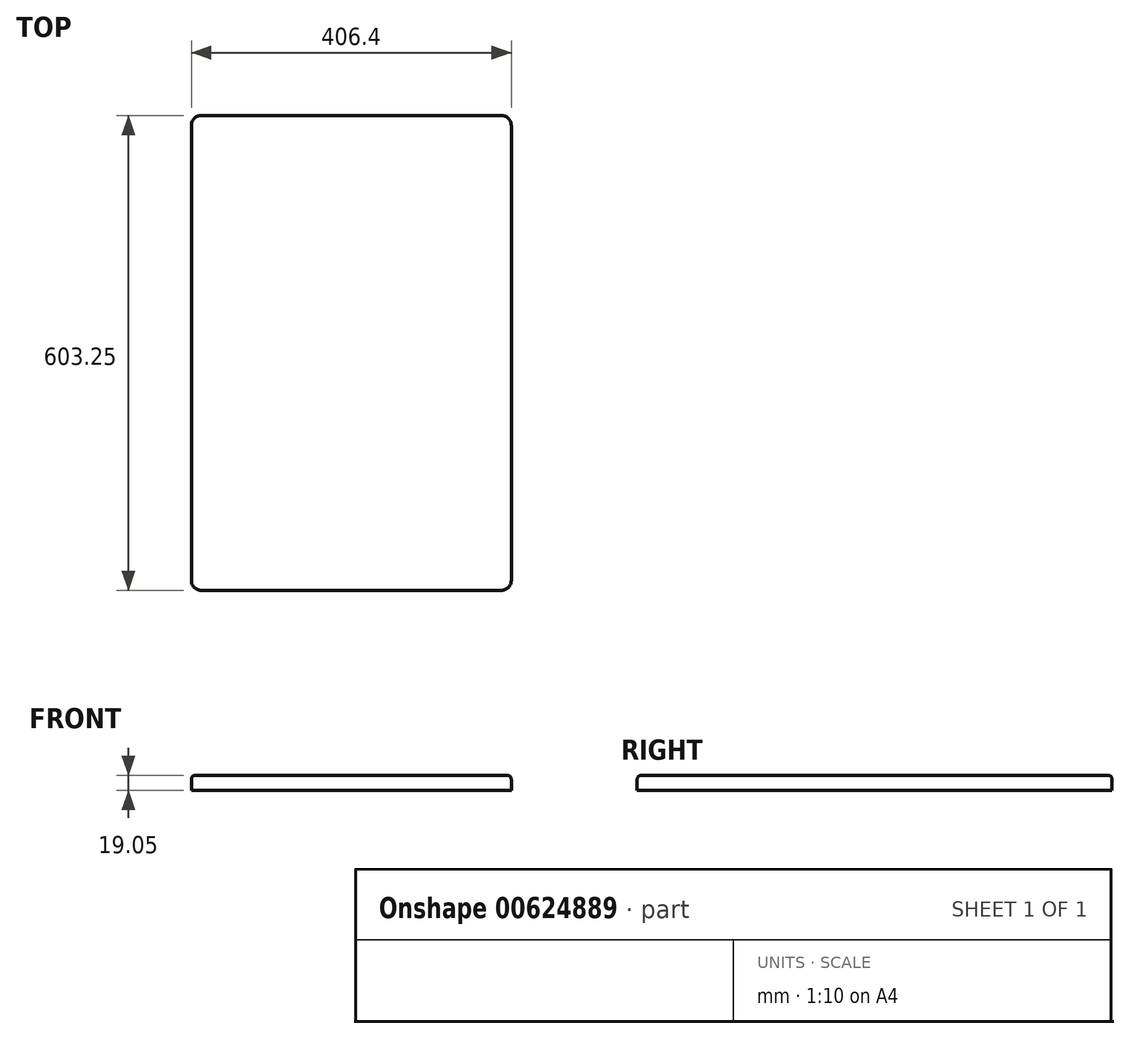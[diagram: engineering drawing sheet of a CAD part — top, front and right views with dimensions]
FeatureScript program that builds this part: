
annotation { "Feature Type Name" : "Feature", "Feature Type Description" : "" }
export const myFeature = defineFeature(function(context is Context, id is Id, definition is map)
    precondition{}
    {
        {
            var Q0;
            Q0=qCreatedBy(makeId("Top.planeOp"),FACE);
            var sketch = newSketch(context, id + "F0", { "sketchPlane" : qUnion([Q0])});
            skLineSegment(sketch, "E0.bottom", {"start": v(0, 0) * mm, "end": v(-406.4, 0) * mm});
            skLineSegment(sketch, "E0.top", {"start": v(0, 603.25) * mm, "end": v(-406.4, 603.25) * mm});
            skLineSegment(sketch, "E0.left", {"start": v(0, 0) * mm, "end": v(0, 603.25) * mm});
            skLineSegment(sketch, "E0.right", {"start": v(-406.4, 0) * mm, "end": v(-406.4, 603.25) * mm});
            skSolve(sketch);
        }
        {
            var Q0;
            Q0=makeQuery(id+"F0.imprint","IMPRINT",FACE,{"disambiguationData":[TD([[makeQuery(id+"F0.imprint","IMPRINT",EDGE,{"derivedFrom":sQuery(id+"F0.wireOp",EDGE,"E0.bottom")}),-1.0]])]});
            extrude(context, id + "F1", {"entities" : qUnion([Q0]), "depth" : 19.05 * mm, "offsetDistance" : 25.4 * mm});
        }
        {
            var Q0;
            Q0=makeQuery(id+"F1.opExtrude","SWEPT_EDGE",EDGE,{"disambiguationData":[OSD([sQuery(id+"F0.wireOp",EDGE,"E0.bottom"),sQuery(id+"F0.wireOp",EDGE,"E0.right")])]});
            var Q1;
            Q1=makeQuery(id+"F1.opExtrude","SWEPT_EDGE",EDGE,{"disambiguationData":[OSD([sQuery(id+"F0.wireOp",EDGE,"E0.bottom"),sQuery(id+"F0.wireOp",EDGE,"E0.left")])]});
            var Q2;
            Q2=makeQuery(id+"F1.opExtrude","SWEPT_EDGE",EDGE,{"disambiguationData":[OSD([sQuery(id+"F0.wireOp",EDGE,"E0.top"),sQuery(id+"F0.wireOp",EDGE,"E0.left")])]});
            var Q3;
            Q3=makeQuery(id+"F1.opExtrude","SWEPT_EDGE",EDGE,{"disambiguationData":[OSD([sQuery(id+"F0.wireOp",EDGE,"E0.top"),sQuery(id+"F0.wireOp",EDGE,"E0.right")])]});
            fillet(context, id + "F2", {"entities" : qUnion([Q0, Q1, Q2, Q3]), "radius" : 12.7 * mm, "tangentPropagation" : true, "allowEdgeOverflow" : false});
        }
        {
            var Q0;
            Q0=makeQuery(id+"F1.opExtrude","CAP_EDGE",EDGE,{"disambiguationData":[OSD([sQuery(id+"F0.wireOp",EDGE,"E0.bottom")])],"isStart":false});
            fillet(context, id + "F3", {"entities" : qUnion([Q0]), "radius" : 5.08 * mm, "tangentPropagation" : true, "allowEdgeOverflow" : false});
        }
    });
